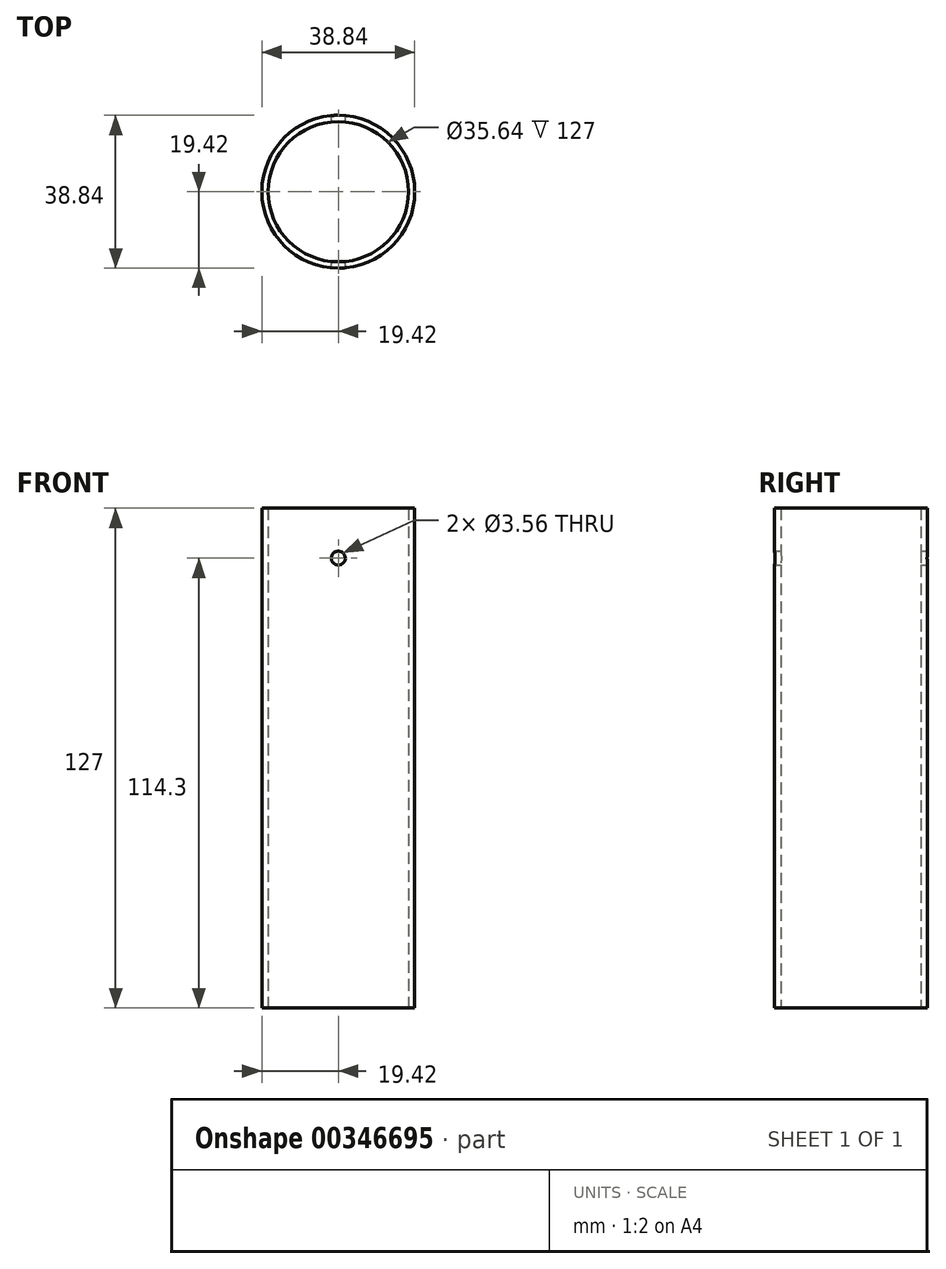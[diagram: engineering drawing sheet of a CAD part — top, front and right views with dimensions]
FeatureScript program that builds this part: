
annotation { "Feature Type Name" : "Feature", "Feature Type Description" : "" }
export const myFeature = defineFeature(function(context is Context, id is Id, definition is map)
    precondition{}
    {
        {
            var Q0;
            Q0=qCreatedBy(makeId("Top.planeOp"),FACE);
            var sketch = newSketch(context, id + "F0", { "sketchPlane" : qUnion([Q0])});
            skCircle(sketch, "E0", {"center": v(0, 0) * mm, "radius": 17.82 * mm});
            skCircle(sketch, "E1", {"center": v(0, 0) * mm, "radius": 19.42 * mm});
            skSolve(sketch);
        }
        {
            var Q0;
            Q0 = qSketchRegion(id + "F0", true);
            extrude(context, id + "F1", {"entities" : qUnion([Q0]), "depth" : 127 * mm});
        }
        {
            var Q0;
            Q0=makeQuery(id+"F1.opExtrude","CAP_FACE",FACE,{"disambiguationData":[OSD([sQuery(id+"F0.wireOp",EDGE,"E0"),sQuery(id+"F0.wireOp",EDGE,"E1")])],"isStart":false});
            var sketch = newSketch(context, id + "F2", { "sketchPlane" : qUnion([Q0])});
            skLineSegment(sketch, "E2", {"start": v(0, 0) * mm, "end": v(0, -19.42) * mm});
            skLineSegment(sketch, "E3", {"start": v(0, -19.42) * mm, "end": v(0, 19.42) * mm});
            skLineSegment(sketch, "E4", {"start": v(0, 19.42) * mm, "end": v(25.4, 19.42) * mm});
            skLineSegment(sketch, "E5", {"start": v(0, -19.42) * mm, "end": v(25.4, -19.42) * mm});
            skSolve(sketch);
        }
        {
            var Q0;
            Q0=sQuery(id+"F2.wireOp",EDGE,"E4");
            cPlane(context, id + "F3", {"entities" : qUnion([Q0]), "cplaneType" : CPlaneType.LINE_ANGLE, "offset" : 25.4 * mm, "angle" : 0 * degree, "width" : 152.4 * mm, "height" : 152.4 * mm});
        }
        {
            var Q0;
            Q0=qCreatedBy(id+"F3.planeOp",FACE);
            var sketch = newSketch(context, id + "F4", { "sketchPlane" : qUnion([Q0])});
            skLineSegment(sketch, "E6", {"start": v(0, 127) * mm, "end": v(0, 114.3) * mm});
            skCircle(sketch, "E7", {"center": v(0, 114.3) * mm, "radius": 1.78 * mm});
            skSolve(sketch);
        }
        {
            var Q0;
            Q0 = qSketchRegion(id + "F4", true);
            extrude(context, id + "F5", {"entities" : qUnion([Q0]), "operationType" : NewBodyOperationType.REMOVE, "endBound" : BoundingType.SYMMETRIC, "oppositeDirection" : true, "depth" : 101.6 * mm});
        }
    });
